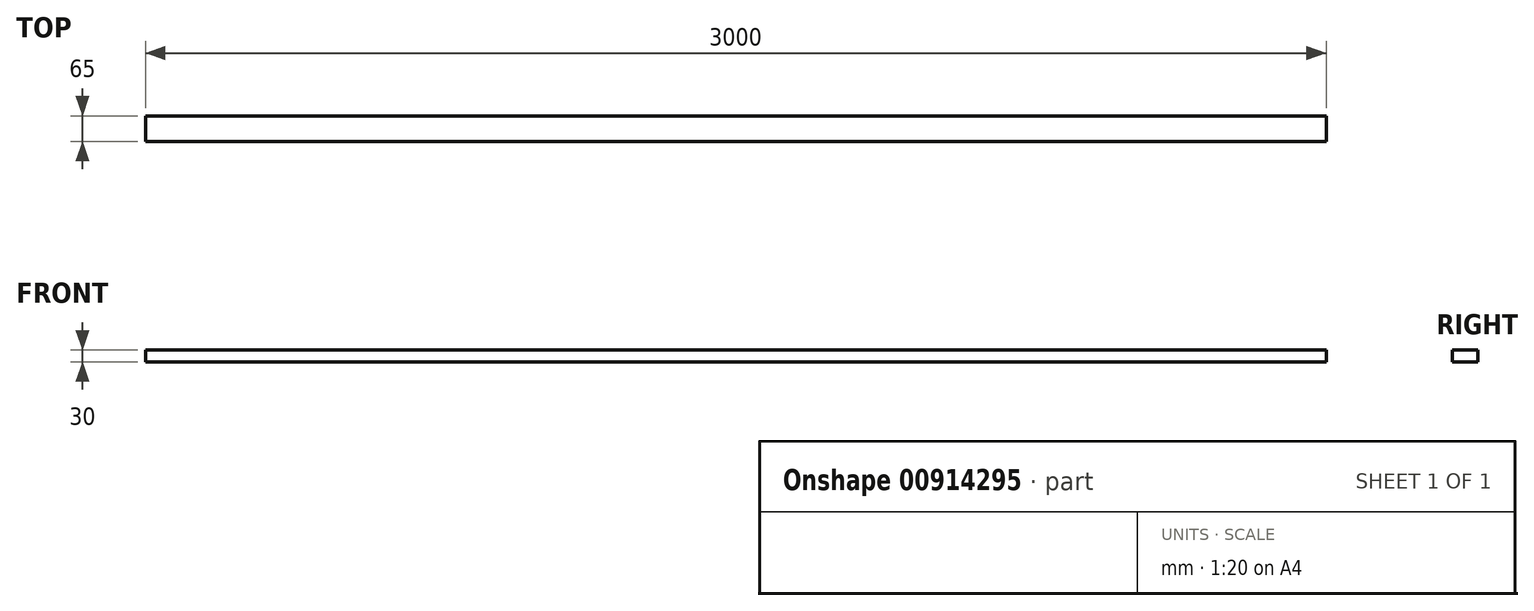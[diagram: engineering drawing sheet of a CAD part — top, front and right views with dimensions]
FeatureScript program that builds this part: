
annotation { "Feature Type Name" : "Feature", "Feature Type Description" : "" }
export const myFeature = defineFeature(function(context is Context, id is Id, definition is map)
    precondition{}
    {
        {
            var Q0;
            Q0=qCreatedBy(makeId("Right.planeOp"),FACE);
            var sketch = newSketch(context, id + "F0", { "sketchPlane" : qUnion([Q0])});
            skLineSegment(sketch, "E0.bottom", {"start": v(32.5, -15) * mm, "end": v(-32.5, -15) * mm});
            skLineSegment(sketch, "E0.top", {"start": v(32.5, 15) * mm, "end": v(-32.5, 15) * mm});
            skLineSegment(sketch, "E0.left", {"start": v(32.5, -15) * mm, "end": v(32.5, 15) * mm});
            skLineSegment(sketch, "E0.right", {"start": v(-32.5, -15) * mm, "end": v(-32.5, 15) * mm});
            skPoint(sketch, "E0.middle", {"position": v(0, 0) * mm});
            skSolve(sketch);
        }
        {
            var Q0;
            Q0 = qSketchRegion(id + "F0", true);
            extrude(context, id + "F1", {"entities" : qUnion([Q0]), "depth" : 3000 * mm, "offsetDistance" : 25 * mm});
        }
    });
